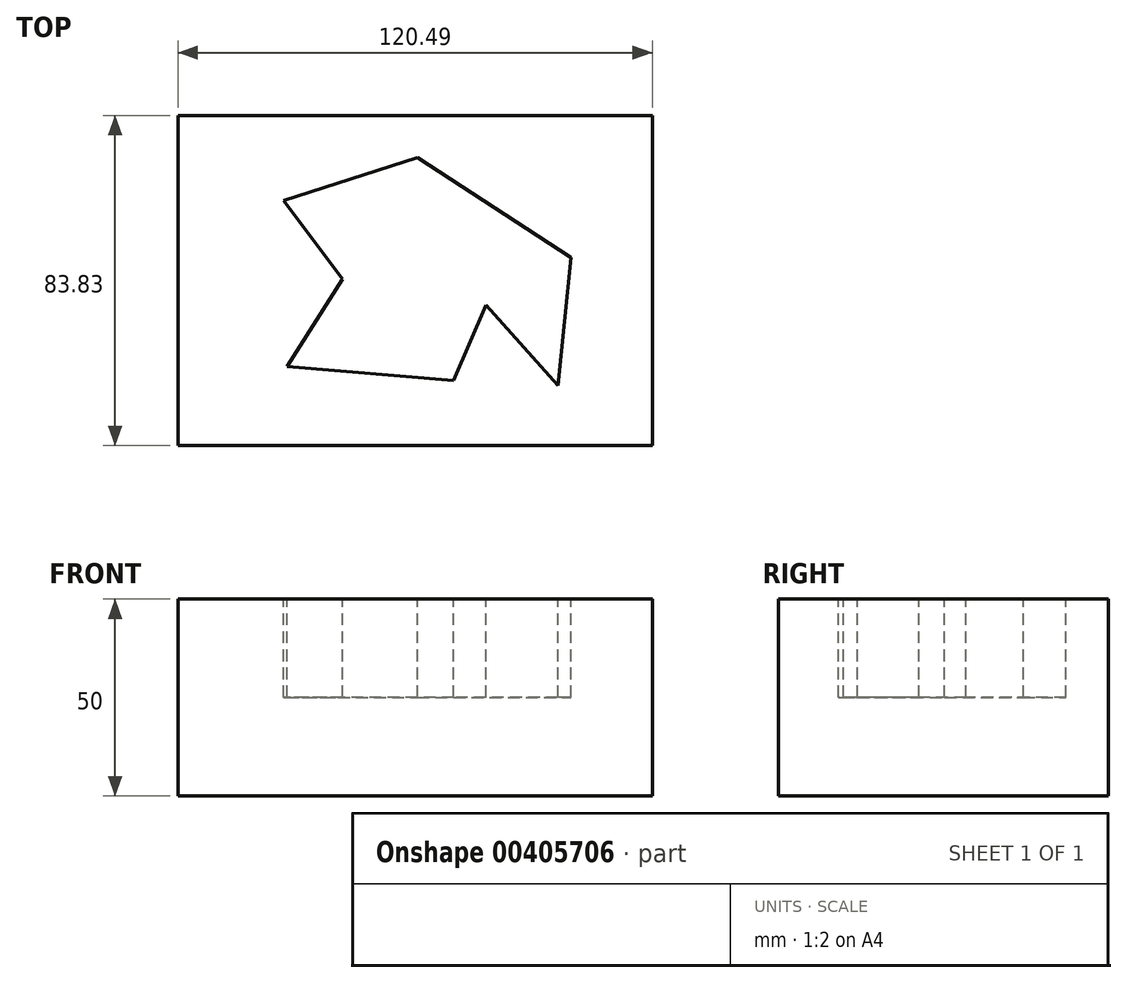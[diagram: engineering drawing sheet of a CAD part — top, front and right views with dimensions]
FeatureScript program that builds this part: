
annotation { "Feature Type Name" : "Feature", "Feature Type Description" : "" }
export const myFeature = defineFeature(function(context is Context, id is Id, definition is map)
    precondition{}
    {
        {
            var Q0;
            Q0=qCreatedBy(makeId("Top.planeOp"),FACE);
            var sketch = newSketch(context, id + "F0", { "sketchPlane" : qUnion([Q0])});
            skLineSegment(sketch, "E0.bottom", {"start": v(-60.79, 48.08) * mm, "end": v(59.7, 48.08) * mm});
            skLineSegment(sketch, "E0.top", {"start": v(-60.79, -35.75) * mm, "end": v(59.7, -35.75) * mm});
            skLineSegment(sketch, "E0.left", {"start": v(-60.79, 48.08) * mm, "end": v(-60.79, -35.75) * mm});
            skLineSegment(sketch, "E0.right", {"start": v(59.7, 48.08) * mm, "end": v(59.7, -35.75) * mm});
            skSolve(sketch);
        }
        {
            var Q0;
            Q0=makeQuery(id+"F0.imprint","IMPRINT",FACE,{"disambiguationData":[TD([[makeQuery(id+"F0.imprint","IMPRINT",EDGE,{"derivedFrom":sQuery(id+"F0.wireOp",EDGE,"E0.bottom")}),-1.0]])]});
            extrude(context, id + "F1", {"entities" : qUnion([Q0]), "depth" : 50 * mm});
        }
        {
            var Q0;
            Q0=makeQuery(id+"F1.opExtrude","CAP_FACE",FACE,{"disambiguationData":[OSD([sQuery(id+"F0.wireOp",EDGE,"E0.bottom"),sQuery(id+"F0.wireOp",EDGE,"E0.top"),sQuery(id+"F0.wireOp",EDGE,"E0.left"),sQuery(id+"F0.wireOp",EDGE,"E0.right")])],"isStart":false});
            var sketch = newSketch(context, id + "F2", { "sketchPlane" : qUnion([Q0])});
            skLineSegment(sketch, "E1", {"start": v(-33.02, -15.6) * mm, "end": v(-19.05, 6.53) * mm});
            skLineSegment(sketch, "E2", {"start": v(-19.05, 6.53) * mm, "end": v(-33.93, 26.5) * mm});
            skLineSegment(sketch, "E3", {"start": v(-33.93, 26.5) * mm, "end": v(0, 37.38) * mm});
            skLineSegment(sketch, "E4", {"start": v(0, 37.38) * mm, "end": v(39.01, 11.98) * mm});
            skLineSegment(sketch, "E5", {"start": v(39.01, 11.98) * mm, "end": v(35.75, -20.5) * mm});
            skLineSegment(sketch, "E6", {"start": v(35.75, -20.5) * mm, "end": v(17.42, 0) * mm});
            skLineSegment(sketch, "E7", {"start": v(17.42, 0) * mm, "end": v(9.25, -19.23) * mm});
            skLineSegment(sketch, "E8", {"start": v(9.25, -19.23) * mm, "end": v(-33.02, -15.6) * mm});
            skSolve(sketch);
        }
        {
            var Q0;
            Q0=makeQuery(id+"F2.imprint","IMPRINT",FACE,{"disambiguationData":[TD([[makeQuery(id+"F2.imprint","IMPRINT",EDGE,{"derivedFrom":sQuery(id+"F2.wireOp",EDGE,"E1")}),-1.0]])]});
            extrude(context, id + "F3", {"entities" : qUnion([Q0]), "operationType" : NewBodyOperationType.REMOVE, "oppositeDirection" : true, "depth" : 25 * mm});
        }
    });
